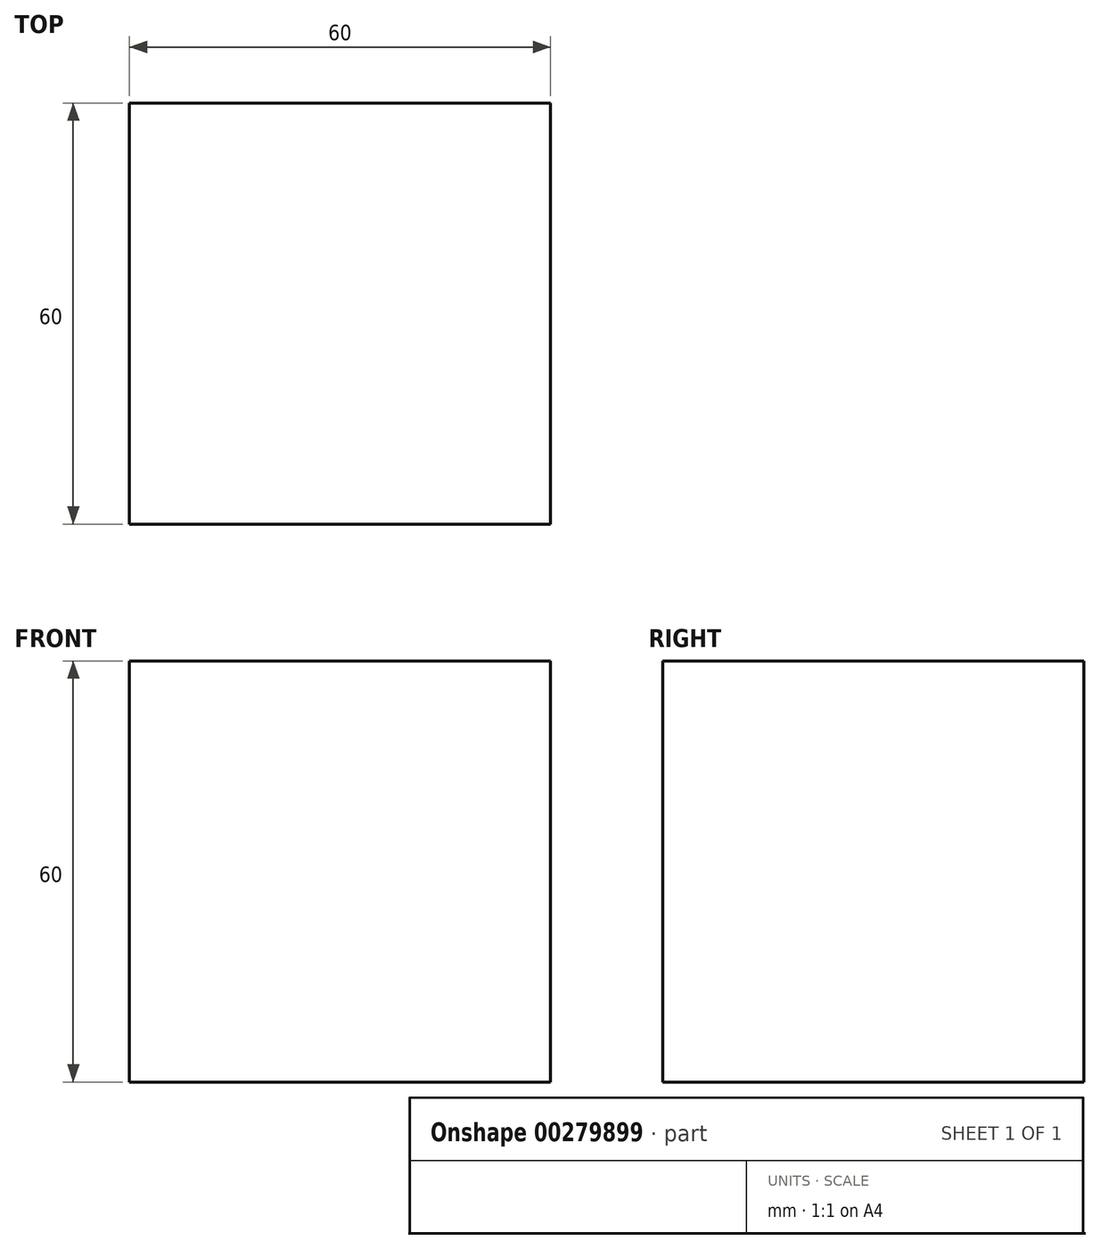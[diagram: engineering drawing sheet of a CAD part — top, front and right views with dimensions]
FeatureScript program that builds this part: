
annotation { "Feature Type Name" : "Feature", "Feature Type Description" : "" }
export const myFeature = defineFeature(function(context is Context, id is Id, definition is map)
    precondition{}
    {
        {
            var Q0;
            Q0=qCreatedBy(makeId("Front.planeOp"),FACE);
            var sketch = newSketch(context, id + "F0", { "sketchPlane" : qUnion([Q0])});
            skLineSegment(sketch, "E0.bottom", {"start": v(0, 0) * mm, "end": v(60, 0) * mm});
            skLineSegment(sketch, "E0.top", {"start": v(0, 60) * mm, "end": v(60, 60) * mm});
            skLineSegment(sketch, "E0.left", {"start": v(0, 0) * mm, "end": v(0, 60) * mm});
            skLineSegment(sketch, "E0.right", {"start": v(60, 0) * mm, "end": v(60, 60) * mm});
            skSolve(sketch);
        }
        {
            var Q0;
            Q0=makeQuery(id+"F0.imprint","IMPRINT",FACE,{"disambiguationData":[TD([[makeQuery(id+"F0.imprint","IMPRINT",EDGE,{"derivedFrom":sQuery(id+"F0.wireOp",EDGE,"E0.bottom")}),1.0]])]});
            extrude(context, id + "F1", {"entities" : qUnion([Q0]), "depth" : 60 * mm});
        }
        {
            var Q0;
            Q0=qCreatedBy(makeId("Front.planeOp"),FACE);
            var sketch = newSketch(context, id + "F2", { "sketchPlane" : qUnion([Q0])});
            skLineSegment(sketch, "E1.bottom", {"start": v(19.1, 17.64) * mm, "end": v(46.69, 17.64) * mm});
            skLineSegment(sketch, "E1.top", {"start": v(19.1, 45.23) * mm, "end": v(46.69, 45.23) * mm});
            skLineSegment(sketch, "E1.left", {"start": v(19.1, 17.64) * mm, "end": v(19.1, 45.23) * mm});
            skLineSegment(sketch, "E1.right", {"start": v(46.69, 17.64) * mm, "end": v(46.69, 45.23) * mm});
            skSolve(sketch);
        }
    });
